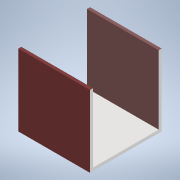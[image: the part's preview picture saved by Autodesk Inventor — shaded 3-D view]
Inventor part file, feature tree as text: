
AUTODESK INVENTOR PART (.ipt)
format: ipt  version: 2022.3 (Build 263350000, 350)  size: 123,904 bytes
history: native  units: in
note: dims shown in document units (in); Inventor stores cm internally (conversion verified against a paired STEP export)
features: extrude x3, sketch x3
ambient origin geometry x8: Origin, YZ Plane, XZ Plane, XY Plane, X Axis, Y Axis, Z Axis, Center Point
bodies: Solid1 (feature_tree)
feature tree (6):
  extrude  "Extrusion1"  Depth=11.8in
  extrude  "Extrusion2"  Depth=0.5in
  extrude  "Extrusion3"  Depth=0.5in
  sketch  "Sketch1"  dims[d0=11.8in d1=11.8in]
  sketch  "Sketch2"  dims[d2=0.5in d3=0.0in d4=0.5in]
  sketch  "Sketch3"  dims[d5=11.3in d6=0.0in d7=0.5in d8=11.3in d9=0.0in]
